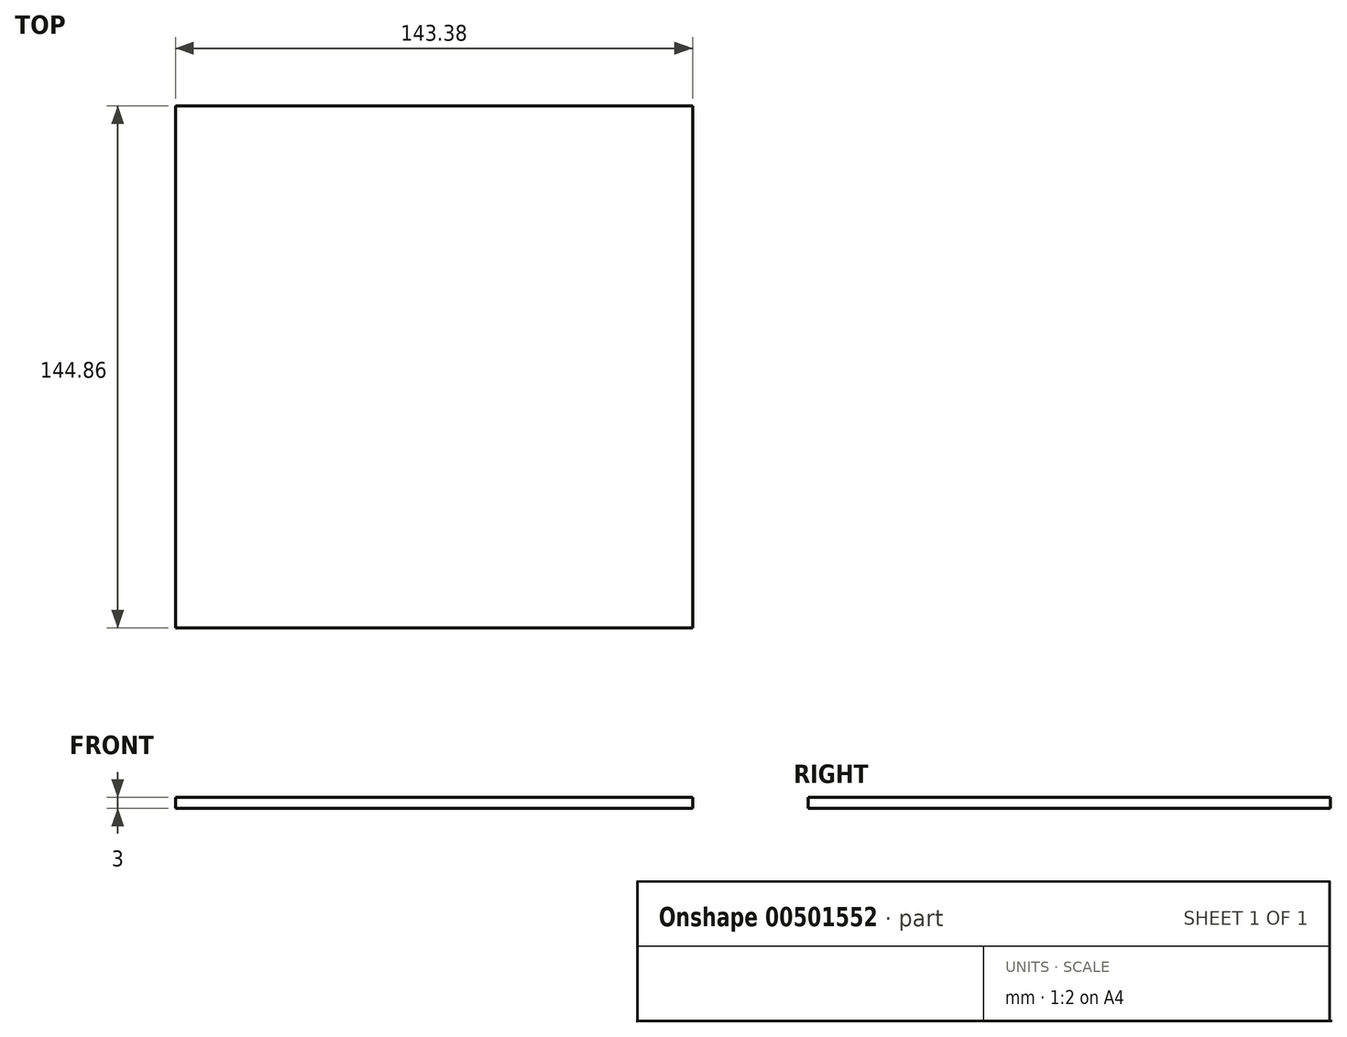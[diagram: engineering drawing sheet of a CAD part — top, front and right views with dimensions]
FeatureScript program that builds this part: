
annotation { "Feature Type Name" : "Feature", "Feature Type Description" : "" }
export const myFeature = defineFeature(function(context is Context, id is Id, definition is map)
    precondition{}
    {
        {
            var Q0;
            Q0=qCreatedBy(makeId("Top.planeOp"),FACE);
            var sketch = newSketch(context, id + "F0", { "sketchPlane" : qUnion([Q0])});
            skLineSegment(sketch, "E0.bottom", {"start": v(71.7, 72.43) * mm, "end": v(-71.7, 72.43) * mm});
            skLineSegment(sketch, "E0.top", {"start": v(71.7, -72.43) * mm, "end": v(-71.7, -72.43) * mm});
            skLineSegment(sketch, "E0.left", {"start": v(71.7, 72.43) * mm, "end": v(71.7, -72.43) * mm});
            skLineSegment(sketch, "E0.right", {"start": v(-71.7, 72.43) * mm, "end": v(-71.7, -72.43) * mm});
            skPoint(sketch, "E0.middle", {"position": v(0, 0) * mm});
            skSolve(sketch);
        }
        {
            var Q0;
            Q0=makeQuery(id+"F0.imprint","IMPRINT",FACE,{"disambiguationData":[TD([[makeQuery(id+"F0.imprint","IMPRINT",EDGE,{"derivedFrom":sQuery(id+"F0.wireOp",EDGE,"E0.bottom")}),1.0]])]});
            extrude(context, id + "F1", {"entities" : qUnion([Q0]), "depth" : 3 * mm});
        }
    });
